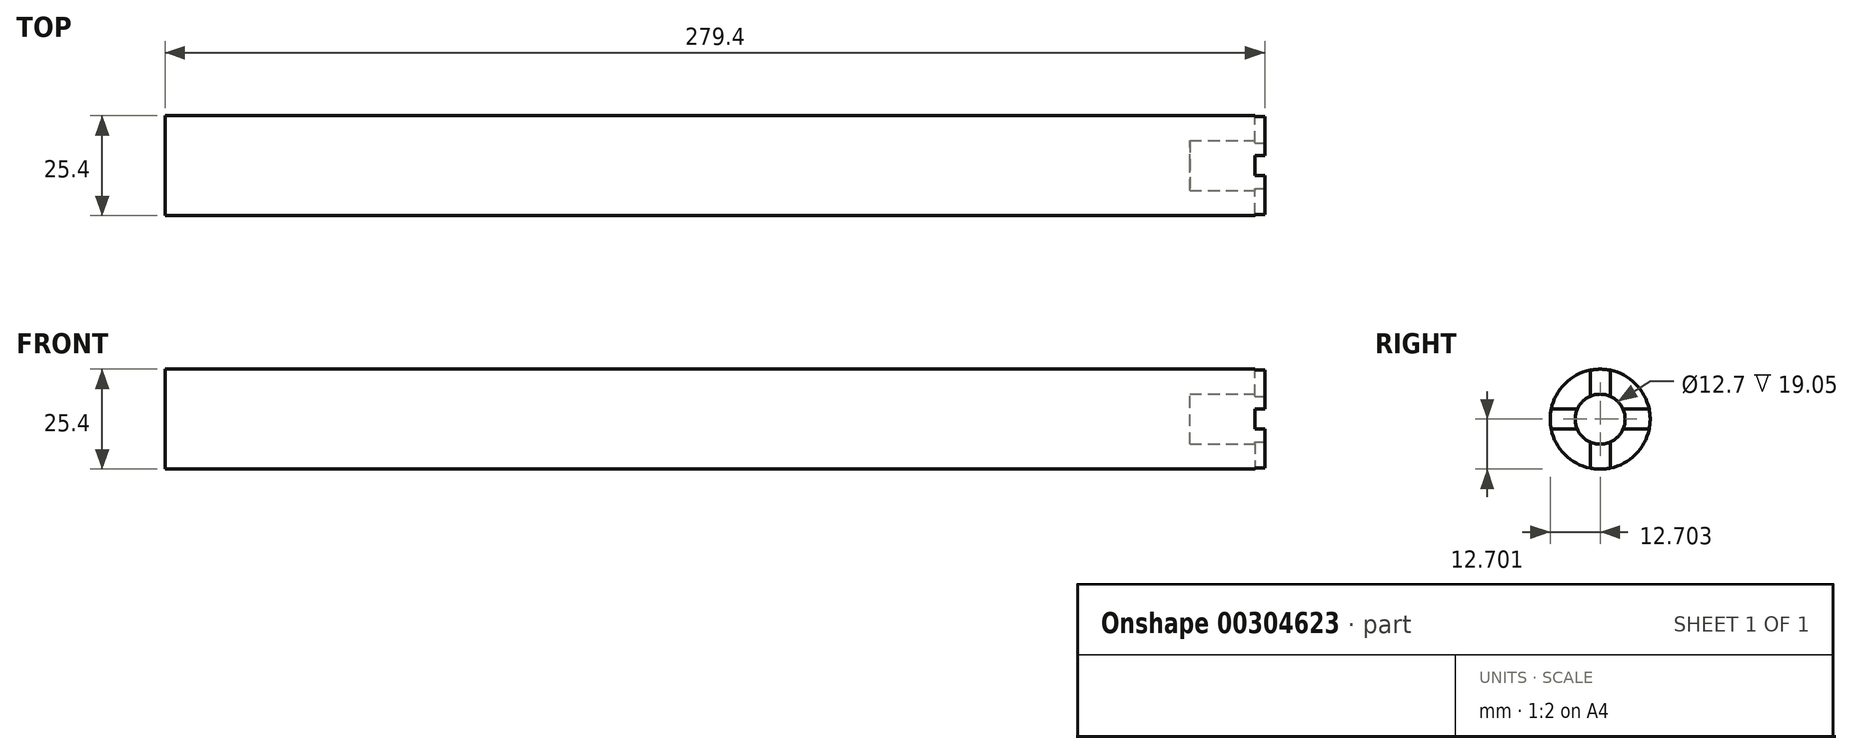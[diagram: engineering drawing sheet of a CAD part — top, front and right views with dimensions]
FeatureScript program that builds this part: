
annotation { "Feature Type Name" : "Feature", "Feature Type Description" : "" }
export const myFeature = defineFeature(function(context is Context, id is Id, definition is map)
    precondition{}
    {
        {
            var Q0;
            Q0=qCreatedBy(makeId("Right.planeOp"),FACE);
            var sketch = newSketch(context, id + "F0", { "sketchPlane" : qUnion([Q0])});
            skCircle(sketch, "E0", {"center": v(27.46, -22.47) * mm, "radius": 12.7 * mm});
            skSolve(sketch);
        }
        {
            var Q0;
            Q0=makeQuery(id+"F0.imprint","IMPRINT",FACE,{"disambiguationData":[TD([[makeQuery(id+"F0.imprint","IMPRINT",EDGE,{"derivedFrom":sQuery(id+"F0.wireOp",EDGE,"E0")}),1.0]])]});
            extrude(context, id + "F1", {"entities" : qUnion([Q0]), "oppositeDirection" : true, "depth" : 279.4 * mm});
        }
        {
            var Q0;
            Q0=makeQuery(id+"F1.opExtrude","CAP_FACE",FACE,{"disambiguationData":[OSD([sQuery(id+"F0.wireOp",EDGE,"E0")])],"isStart":true});
            var sketch = newSketch(context, id + "F2", { "sketchPlane" : qUnion([Q0])});
            skLineSegment(sketch, "E1", {"start": v(30, -28.29) * mm, "end": v(30, -34.91) * mm});
            skLineSegment(sketch, "E2.MirrorCS", {"start": v(24.92, -28.29) * mm, "end": v(24.92, -34.91) * mm});
            skCircle(sketch, "E3", {"center": v(27.46, -22.47) * mm, "radius": 6.35 * mm});
            skLineSegment(sketch, "E4.MirrorCS", {"start": v(30, -16.65) * mm, "end": v(30, -10.03) * mm});
            skLineSegment(sketch, "E5.MirrorCS", {"start": v(24.92, -16.65) * mm, "end": v(24.92, -10.03) * mm});
            skLineSegment(sketch, "E6", {"start": v(33.28, -19.93) * mm, "end": v(39.9, -19.93) * mm});
            skLineSegment(sketch, "E7.MirrorCS", {"start": v(33.28, -25) * mm, "end": v(39.9, -25) * mm});
            skLineSegment(sketch, "E8", {"start": v(15.02, -25) * mm, "end": v(21.64, -25) * mm});
            skLineSegment(sketch, "E9", {"start": v(21.64, -19.93) * mm, "end": v(15.02, -19.93) * mm});
            skPoint(sketch, "E10.start.orphan", {"position": v(40.16, -22.47) * mm});
            skSolve(sketch);
        }
        {
            var Q0;
            {var subQ0=sQuery(id+"F2.wireOp",EDGE,"E3");var subQ4=makeQuery(id+"F2.imprint","INTERSECT",VERTEX,{"derivedFrom":[subQ0,sQuery(id+"F2.wireOp",EDGE,"E4.MirrorCS")]});Q0=makeQuery(id+"F2.imprint","IMPRINT",FACE,{"disambiguationData":[TD([[makeQuery(id+"F2.imprint","IMPRINT",EDGE,{"disambiguationData":[TD([[subQ4,1.0]])],"derivedFrom":subQ0}),1.0]])]});}
            extrude(context, id + "F3", {"entities" : qUnion([Q0]), "operationType" : NewBodyOperationType.REMOVE, "oppositeDirection" : true, "depth" : 19.05 * mm});
        }
        {
            var Q0;
            {var subQ0=sQuery(id+"F2.wireOp",EDGE,"E8");Q0=makeQuery(id+"F2.imprint","IMPRINT",FACE,{"disambiguationData":[TD([[makeQuery(id+"F2.imprint","IMPRINT",EDGE,{"derivedFrom":subQ0}),1.0]])]});}
            var Q1;
            {var subQ0=sQuery(id+"F2.wireOp",EDGE,"E4.MirrorCS");Q1=makeQuery(id+"F2.imprint","IMPRINT",FACE,{"disambiguationData":[TD([[makeQuery(id+"F2.imprint","IMPRINT",EDGE,{"derivedFrom":subQ0}),1.0]])]});}
            var Q2;
            {var subQ0=sQuery(id+"F2.wireOp",EDGE,"E6");Q2=makeQuery(id+"F2.imprint","IMPRINT",FACE,{"disambiguationData":[TD([[makeQuery(id+"F2.imprint","IMPRINT",EDGE,{"derivedFrom":subQ0}),-1.0]])]});}
            var Q3;
            {var subQ0=sQuery(id+"F2.wireOp",EDGE,"E1");Q3=makeQuery(id+"F2.imprint","IMPRINT",FACE,{"disambiguationData":[TD([[makeQuery(id+"F2.imprint","IMPRINT",EDGE,{"derivedFrom":subQ0}),-1.0]])]});}
            extrude(context, id + "F4", {"entities" : qUnion([Q0, Q1, Q2, Q3]), "operationType" : NewBodyOperationType.REMOVE, "oppositeDirection" : true, "depth" : 2.54 * mm});
        }
    });
